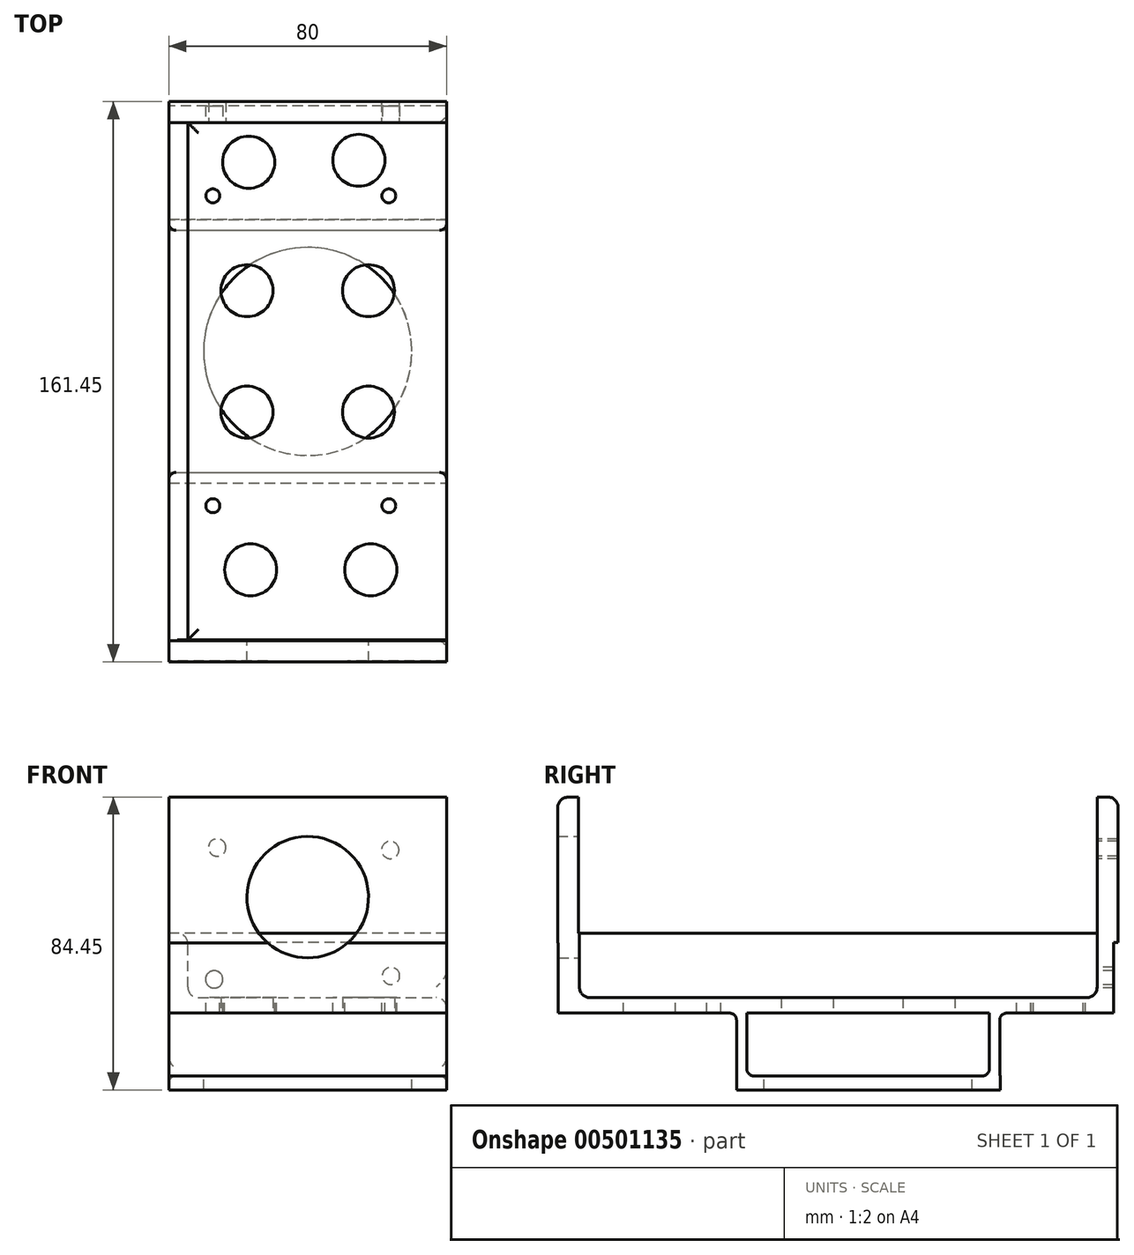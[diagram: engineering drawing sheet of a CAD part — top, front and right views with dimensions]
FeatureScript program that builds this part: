
annotation { "Feature Type Name" : "Feature", "Feature Type Description" : "" }
export const myFeature = defineFeature(function(context is Context, id is Id, definition is map)
    precondition{}
    {
        {
            var Q0;
            Q0=qCreatedBy(makeId("Right.planeOp"),FACE);
            cPlane(context, id + "F0", {"entities" : qUnion([Q0]), "cplaneType" : CPlaneType.OFFSET, "offset" : 40 * mm, "width" : 150 * mm, "height" : 150 * mm});
        }
        {
            var Q0;
            Q0=qCreatedBy(id+"F0.planeOp",FACE);
            var sketch = newSketch(context, id + "F1", { "sketchPlane" : qUnion([Q0])});
            skLineSegment(sketch, "E0.bottom", {"start": v(-37.9, -30.8) * mm, "end": v(38.1, -30.8) * mm});
            skLineSegment(sketch, "E0.top", {"start": v(-37.9, -34.8) * mm, "end": v(38.1, -34.8) * mm});
            skLineSegment(sketch, "E0.left", {"start": v(-37.9, -30.8) * mm, "end": v(-37.9, -34.8) * mm});
            skLineSegment(sketch, "E0.right", {"start": v(38.1, -30.8) * mm, "end": v(38.1, -34.8) * mm});
            skLineSegment(sketch, "E1.bottom", {"start": v(-37.92, -9.8) * mm, "end": v(-34.92, -9.8) * mm});
            skLineSegment(sketch, "E1.top", {"start": v(-37.92, -30.8) * mm, "end": v(-34.92, -30.8) * mm});
            skLineSegment(sketch, "E1.left", {"start": v(-37.92, -9.8) * mm, "end": v(-37.92, -30.8) * mm});
            skLineSegment(sketch, "E1.right", {"start": v(-34.92, -9.8) * mm, "end": v(-34.92, -30.8) * mm});
            skLineSegment(sketch, "E2.MirrorCS", {"start": v(34.92, -9.8) * mm, "end": v(34.92, -30.8) * mm});
            skLineSegment(sketch, "E3.MirrorCS", {"start": v(37.92, -9.8) * mm, "end": v(34.92, -9.8) * mm});
            skLineSegment(sketch, "E4.MirrorCS", {"start": v(37.92, -9.8) * mm, "end": v(37.92, -30.8) * mm});
            skLineSegment(sketch, "E5.MirrorCS", {"start": v(37.92, -30.8) * mm, "end": v(34.92, -30.8) * mm});
            skLineSegment(sketch, "E6.bottom", {"start": v(-89.28, 10.32) * mm, "end": v(70.72, 10.32) * mm});
            skLineSegment(sketch, "E6.top", {"start": v(-89.28, -12.68) * mm, "end": v(70.72, -12.68) * mm});
            skLineSegment(sketch, "E6.left", {"start": v(-89.28, 10.32) * mm, "end": v(-89.28, -12.68) * mm});
            skLineSegment(sketch, "E6.right", {"start": v(70.72, 10.32) * mm, "end": v(70.72, -12.68) * mm});
            skSolve(sketch);
        }
        {
            var Q0;
            Q0=qSketchRegion(id+"F1",true);
            var Q1;
            Q1=qConstructionFilter(qBodyType(qCreatedBy(id+"F1",EDGE),BodyType.WIRE),ConstructionObject.NO);
            extrude(context, id + "F2", {"entities" : qUnion([Q0]), "surfaceEntities" : qUnion([Q1]), "oppositeDirection" : true, "depth" : 80 * mm});
        }
        {
            var Q0;
            Q0=qCreatedBy(makeId("Top.planeOp"),FACE);
            cPlane(context, id + "F3", {"entities" : qUnion([Q0]), "cplaneType" : CPlaneType.OFFSET, "offset" : 44.8 * mm, "width" : 150 * mm, "height" : 150 * mm});
        }
        {
            var Q0;
            Q0=makeQuery(id+"F2.opExtrude","SWEPT_EDGE",EDGE,{"disambiguationData":[OSD([sQuery(id+"F1.wireOp",EDGE,"8911faaa-2e56-4fcc-9375-60c6f1163b9a0.MirrorCS"),sQuery(id+"F1.wireOp",EDGE,"a3ff945b-d483-49d8-b67e-3c9789cdbadf0.MirrorCS")])]});
            var Q1;
            Q1=makeQuery(id+"F2.opExtrude","SWEPT_EDGE",EDGE,{"disambiguationData":[OSD([sQuery(id+"F1.wireOp",EDGE,"KpOeElVU-bQIC-6Ijm-ua4u-k8ctu78gNPEQ.bottom"),sQuery(id+"F1.wireOp",EDGE,"KpOeElVU-bQIC-6Ijm-ua4u-k8ctu78gNPEQ.right")])]});
            var Q2;
            Q2=makeQuery(id+"F2.opExtrude","SWEPT_EDGE",EDGE,{"disambiguationData":[OSD([sQuery(id+"F1.wireOp",EDGE,"E0.bottom"),sQuery(id+"F1.wireOp",EDGE,"E5.MirrorCS"),sQuery(id+"F1.wireOp",EDGE,"E2.MirrorCS")])]});
            var Q3;
            Q3=makeQuery(id+"F2.opExtrude","SWEPT_EDGE",EDGE,{"disambiguationData":[OSD([sQuery(id+"F1.wireOp",EDGE,"E0.bottom"),sQuery(id+"F1.wireOp",EDGE,"E1.top"),sQuery(id+"F1.wireOp",EDGE,"E1.right")])]});
            var Q4;
            Q4=makeQuery(id+"F2.opExtrude","SWEPT_EDGE",EDGE,{"disambiguationData":[OSD([sQuery(id+"F1.wireOp",EDGE,"E1.left"),sQuery(id+"F1.wireOp",EDGE,"KpOeElVU-bQIC-6Ijm-ua4u-k8ctu78gNPEQ.top")])]});
            var Q5;
            Q5=makeQuery(id+"F2.opExtrude","SWEPT_EDGE",EDGE,{"disambiguationData":[OSD([sQuery(id+"F1.wireOp",EDGE,"E4.MirrorCS"),sQuery(id+"F1.wireOp",EDGE,"63763e1a-3015-4774-828e-56aecf1c89e60.MirrorCS")])]});
            var Q6;
            {var subQ0=sQuery(id+"F1.wireOp",EDGE,"E0.bottom");Q6=makeQuery(id+"F2.opExtrude","CAP_EDGE",EDGE,{"disambiguationData":[OSD([subQ0]),TDD([makeQuery(id+"F1.imprint","IMPRINT",EDGE,{"disambiguationData":[TD([[makeQuery(id+"F1.imprint","INTERSECT",VERTEX,{"derivedFrom":[subQ0,sQuery(id+"F1.wireOp",EDGE,"E1.top"),sQuery(id+"F1.wireOp",EDGE,"E1.right")]}),-1.0]])],"derivedFrom":subQ0})])],"isStart":false});}
            var Q7;
            {var subQ0=sQuery(id+"F1.wireOp",EDGE,"E0.bottom");Q7=makeQuery(id+"F2.opExtrude","CAP_EDGE",EDGE,{"disambiguationData":[OSD([subQ0]),TDD([makeQuery(id+"F1.imprint","IMPRINT",EDGE,{"disambiguationData":[TD([[makeQuery(id+"F1.imprint","INTERSECT",VERTEX,{"derivedFrom":[subQ0,sQuery(id+"F1.wireOp",EDGE,"E1.top"),sQuery(id+"F1.wireOp",EDGE,"E1.right")]}),-1.0]])],"derivedFrom":subQ0})])],"isStart":true});}
            fillet(context, id + "F4", {"entities" : qUnion([Q0, Q1, Q2, Q3, Q4, Q5, Q6, Q7]), "radius" : 2 * mm, "tangentPropagation" : true, "allowEdgeOverflow" : false});
        }
        {
            var Q0;
            Q0=qCreatedBy(makeId("Top.planeOp"),FACE);
            cPlane(context, id + "F5", {"entities" : qUnion([Q0]), "cplaneType" : CPlaneType.OFFSET, "offset" : 12.9 * mm, "width" : 150 * mm, "height" : 150 * mm});
        }
        {
            var Q0;
            Q0=qCreatedBy(id+"F5.planeOp",FACE);
            var sketch = newSketch(context, id + "F6", { "sketchPlane" : qUnion([Q0])});
            skPoint(sketch, "E7", {"position": v(-27.34, 44.84) * mm});
            skLineSegment(sketch, "E8", {"start": v(-2, 0.18) * mm, "end": v(-2, 48.05) * mm});
            skLineSegment(sketch, "E9", {"start": v(-2, 48.05) * mm, "end": v(-2, 0.18) * mm, "construction": true});
            skLineSegment(sketch, "E10", {"start": v(-2, 0.18) * mm, "end": v(-2, -49.46) * mm});
            skLineSegment(sketch, "E11", {"start": v(-2, 0.18) * mm, "end": v(39.06, 0.18) * mm});
            skLineSegment(sketch, "E12", {"start": v(39.06, 0.18) * mm, "end": v(-44.25, 0.18) * mm, "construction": true});
            skPoint(sketch, "E13.MirrorP", {"position": v(23.36, 44.84) * mm});
            skLineSegment(sketch, "E14.MirrorCS", {"start": v(-2, 0.18) * mm, "end": v(-2, -49.46) * mm, "construction": true});
            skPoint(sketch, "E15.MirrorP", {"position": v(-27.34, -44.5) * mm});
            skPoint(sketch, "E16.MirrorP", {"position": v(23.36, -44.5) * mm});
            skSolve(sketch);
        }
        {
            var Q0;
            Q0=sQuery(id+"F6.wireOp",VERTEX,"E16.MirrorP");
            var Q1;
            Q1=sQuery(id+"F6.wireOp",VERTEX,"E15.MirrorP");
            var Q2;
            Q2=sQuery(id+"F6.wireOp",VERTEX,"E7");
            var Q3;
            Q3=sQuery(id+"F6.wireOp",VERTEX,"E13.MirrorP");
            var Q4;
            Q4=makeQuery(id+"F2.opExtrude","SWEPT_BODY",BODY,{"disambiguationData":[OSD([sQuery(id+"F1.wireOp",EDGE,"E0.bottom"),sQuery(id+"F1.wireOp",EDGE,"E0.top"),sQuery(id+"F1.wireOp",EDGE,"E0.left"),sQuery(id+"F1.wireOp",EDGE,"E0.right"),sQuery(id+"F1.wireOp",EDGE,"E1.top"),sQuery(id+"F1.wireOp",EDGE,"E1.left"),sQuery(id+"F1.wireOp",EDGE,"E1.right"),sQuery(id+"F1.wireOp",EDGE,"E4.MirrorCS"),sQuery(id+"F1.wireOp",EDGE,"E2.MirrorCS"),sQuery(id+"F1.wireOp",EDGE,"E6.bottom"),sQuery(id+"F1.wireOp",EDGE,"E6.top"),sQuery(id+"F1.wireOp",EDGE,"E6.left"),sQuery(id+"F1.wireOp",EDGE,"E6.right")])]});
            hole(context, id + "F7", {"style" : HoleStyle.SIMPLE, "endStyle" : HoleEndStyle.BLIND, "holeDiameter" : 4 * mm, "holeDepth" : 25 * mm, "isTappedThrough" : true, "tappedDepth" : 12 * mm, "tapClearance" : 3, "locations" : qUnion([Q0, Q1, Q2, Q3]), "scope" : qUnion([Q4])});
        }
        {
            var Q0;
            Q0=qCreatedBy(makeId("Top.planeOp"),FACE);
            cPlane(context, id + "F8", {"entities" : qUnion([Q0]), "cplaneType" : CPlaneType.OFFSET, "offset" : 12.8 * mm, "width" : 150 * mm, "height" : 150 * mm});
        }
        {
            var Q0;
            Q0=qCreatedBy(id+"F8.planeOp",FACE);
            var sketch = newSketch(context, id + "F9", { "sketchPlane" : qUnion([Q0])});
            skLineSegment(sketch, "E17.bottom", {"start": v(-39.53, 72.98) * mm, "end": v(-34.53, 72.98) * mm, "construction": true});
            skLineSegment(sketch, "E17.top", {"start": v(-39.53, 65.98) * mm, "end": v(-34.53, 65.98) * mm, "construction": true});
            skLineSegment(sketch, "E17.left", {"start": v(-39.53, 72.98) * mm, "end": v(-39.53, 65.98) * mm, "construction": true});
            skLineSegment(sketch, "E17.right", {"start": v(-34.53, 72.98) * mm, "end": v(-34.53, 65.98) * mm, "construction": true});
            skLineSegment(sketch, "E18.bottom", {"start": v(-40.05, -95.1) * mm, "end": v(-35.05, -95.1) * mm, "construction": true});
            skLineSegment(sketch, "E18.top", {"start": v(-40.05, -102.1) * mm, "end": v(-35.05, -102.1) * mm, "construction": true});
            skLineSegment(sketch, "E18.left", {"start": v(-40.05, -95.1) * mm, "end": v(-40.05, -102.1) * mm, "construction": true});
            skLineSegment(sketch, "E18.right", {"start": v(-35.05, -95.1) * mm, "end": v(-35.05, -102.1) * mm, "construction": true});
            skLineSegment(sketch, "E19.bottom", {"start": v(40.15, 72.98) * mm, "end": v(47.15, 72.98) * mm, "construction": true});
            skLineSegment(sketch, "E19.top", {"start": v(40.15, 65.98) * mm, "end": v(47.15, 65.98) * mm, "construction": true});
            skLineSegment(sketch, "E19.left", {"start": v(40.15, 72.98) * mm, "end": v(40.15, 65.98) * mm, "construction": true});
            skLineSegment(sketch, "E19.right", {"start": v(47.15, 72.98) * mm, "end": v(47.15, 65.98) * mm, "construction": true});
            skLineSegment(sketch, "E20.bottom", {"start": v(-34.53, 65.98) * mm, "end": v(40.15, 65.98) * mm});
            skLineSegment(sketch, "E20.top", {"start": v(-34.53, -83.16) * mm, "end": v(40.15, -83.16) * mm});
            skLineSegment(sketch, "E20.left", {"start": v(-34.53, 65.98) * mm, "end": v(-34.53, -83.16) * mm});
            skLineSegment(sketch, "E20.right", {"start": v(40.15, 65.98) * mm, "end": v(40.15, -83.16) * mm});
            skSolve(sketch);
        }
        {
            var Q0;
            Q0 = qSketchRegion(id + "F9", true);
            extrude(context, id + "F10", {"entities" : qUnion([Q0]), "operationType" : NewBodyOperationType.REMOVE, "oppositeDirection" : true, "depth" : 21 * mm});
        }
        {
            var Q0;
            Q0=qCreatedBy(makeId("Right.planeOp"),FACE);
            var sketch = newSketch(context, id + "F11", { "sketchPlane" : qUnion([Q0])});
            skLineSegment(sketch, "E21.bottom", {"start": v(-89.45, 7.56) * mm, "end": v(-83.45, 7.56) * mm});
            skLineSegment(sketch, "E21.top", {"start": v(-89.45, 49.56) * mm, "end": v(-83.45, 49.56) * mm});
            skLineSegment(sketch, "E21.left", {"start": v(-89.45, 7.56) * mm, "end": v(-89.45, 49.56) * mm});
            skLineSegment(sketch, "E21.right", {"start": v(-83.45, 7.56) * mm, "end": v(-83.45, 49.56) * mm});
            skLineSegment(sketch, "E22.bottom", {"start": v(66, 7.64) * mm, "end": v(72, 7.64) * mm});
            skLineSegment(sketch, "E22.top", {"start": v(66, 49.64) * mm, "end": v(72, 49.64) * mm});
            skLineSegment(sketch, "E22.left", {"start": v(66, 7.64) * mm, "end": v(66, 49.64) * mm});
            skLineSegment(sketch, "E22.right", {"start": v(72, 7.64) * mm, "end": v(72, 49.64) * mm});
            skSolve(sketch);
        }
        {
            var Q0;
            Q0 = qSketchRegion(id + "F11", true);
            extrude(context, id + "F12", {"entities" : qUnion([Q0]), "operationType" : NewBodyOperationType.ADD, "endBound" : BoundingType.SYMMETRIC, "depth" : 80 * mm});
        }
        {
            var Q0;
            Q0=qCreatedBy(makeId("Front.planeOp"),FACE);
            var sketch = newSketch(context, id + "F13", { "sketchPlane" : qUnion([Q0])});
            skCircle(sketch, "E23", {"center": v(-26.09, 35.07) * mm, "radius": 2.5 * mm});
            skLineSegment(sketch, "E24", {"start": v(-26.09, 23.89) * mm, "end": v(-26.09, 0) * mm, "construction": true});
            skLineSegment(sketch, "E25", {"start": v(23.77, 22.73) * mm, "end": v(23.92, 0) * mm, "construction": true});
            skCircle(sketch, "E26", {"center": v(-26.95, -2.95) * mm, "radius": 2.5 * mm});
            skLineSegment(sketch, "E27", {"start": v(-26.95, 1.86) * mm, "end": v(-26.95, -22.03) * mm, "construction": true});
            skLineSegment(sketch, "E28", {"start": v(23.77, 12.22) * mm, "end": v(24, -22.03) * mm, "construction": true});
            skCircle(sketch, "E29", {"center": v(23.77, 34.34) * mm, "radius": 2.5 * mm});
            skLineSegment(sketch, "E30", {"start": v(23.77, 24.59) * mm, "end": v(23.77, 12.22) * mm, "construction": true});
            skLineSegment(sketch, "E31", {"start": v(74.64, 23.43) * mm, "end": v(74.78, 0.7) * mm, "construction": true});
            skCircle(sketch, "E32", {"center": v(23.98, -1.95) * mm, "radius": 2.5 * mm});
            skLineSegment(sketch, "E33", {"start": v(23.98, 2.86) * mm, "end": v(23.98, -21.03) * mm, "construction": true});
            skLineSegment(sketch, "E34", {"start": v(74.78, 1.7) * mm, "end": v(74.92, -21.03) * mm, "construction": true});
            skPoint(sketch, "E35", {"position": v(0, 20.75) * mm});
            skSolve(sketch);
        }
        {
            var Q0;
            Q0=makeQuery(id+"F12.opExtrude","SWEPT_EDGE",EDGE,{"disambiguationData":[OSD([sQuery(id+"F11.wireOp",EDGE,"E21.top"),sQuery(id+"F11.wireOp",EDGE,"E21.left")])]});
            var Q1;
            Q1=makeQuery(id+"F10.boolean.opBoolean","COPY",EDGE,{"derivedFrom":makeQuery(id+"F10.opExtrude","CAP_EDGE",EDGE,{"disambiguationData":[OSD([sQuery(id+"F9.wireOp",EDGE,"E20.top")])],"isStart":false})});
            var Q2;
            Q2=makeQuery(id+"F10.boolean.opBoolean","COPY",EDGE,{"derivedFrom":makeQuery(id+"F10.opExtrude","CAP_EDGE",EDGE,{"disambiguationData":[OSD([sQuery(id+"F9.wireOp",EDGE,"E20.left")])],"isStart":false})});
            var Q3;
            Q3=makeQuery(id+"F10.boolean.opBoolean","INTERSECT",EDGE,{"derivedFrom":[makeQuery(id+"F2.opExtrude","CAP_FACE",FACE,{"disambiguationData":[OSD([sQuery(id+"F1.wireOp",EDGE,"E0.bottom"),sQuery(id+"F1.wireOp",EDGE,"E0.top"),sQuery(id+"F1.wireOp",EDGE,"E0.left"),sQuery(id+"F1.wireOp",EDGE,"E0.right"),sQuery(id+"F1.wireOp",EDGE,"E1.top"),sQuery(id+"F1.wireOp",EDGE,"E1.left"),sQuery(id+"F1.wireOp",EDGE,"E1.right"),sQuery(id+"F1.wireOp",EDGE,"E4.MirrorCS"),sQuery(id+"F1.wireOp",EDGE,"E2.MirrorCS"),sQuery(id+"F1.wireOp",EDGE,"E6.bottom"),sQuery(id+"F1.wireOp",EDGE,"E6.top"),sQuery(id+"F1.wireOp",EDGE,"E6.left"),sQuery(id+"F1.wireOp",EDGE,"E6.right")])],"isStart":true}),makeQuery(id+"F10.opExtrude","CAP_FACE",FACE,{"disambiguationData":[OSD([sQuery(id+"F9.wireOp",EDGE,"E20.bottom"),sQuery(id+"F9.wireOp",EDGE,"E20.top"),sQuery(id+"F9.wireOp",EDGE,"E20.left"),sQuery(id+"F9.wireOp",EDGE,"E20.right")])],"isStart":false})]});
            var Q4;
            Q4=makeQuery(id+"F10.boolean.opBoolean","INTERSECT",EDGE,{"derivedFrom":[makeQuery(id+"F2.opExtrude","SWEPT_FACE",FACE,{"disambiguationData":[OSD([sQuery(id+"F1.wireOp",EDGE,"E6.bottom")])]}),makeQuery(id+"F10.opExtrude","SWEPT_FACE",FACE,{"disambiguationData":[OSD([sQuery(id+"F9.wireOp",EDGE,"E20.left")])]})]});
            var Q5;
            Q5=makeQuery(id+"F12.opExtrude","SWEPT_EDGE",EDGE,{"disambiguationData":[OSD([sQuery(id+"F11.wireOp",EDGE,"E22.top"),sQuery(id+"F11.wireOp",EDGE,"E22.right")])]});
            var Q6;
            Q6=makeQuery(id+"F10.boolean.opBoolean","COPY",EDGE,{"derivedFrom":makeQuery(id+"F10.opExtrude","CAP_EDGE",EDGE,{"disambiguationData":[OSD([sQuery(id+"F9.wireOp",EDGE,"E20.bottom")])],"isStart":false})});
            fillet(context, id + "F14", {"entities" : qUnion([Q0, Q1, Q2, Q3, Q4, Q5, Q6]), "radius" : 3 * mm, "tangentPropagation" : true, "allowEdgeOverflow" : false});
        }
        {
            var Q0;
            Q0=sQuery(id+"F13.wireOp",VERTEX,"E29.center");
            var Q1;
            Q1=sQuery(id+"F13.wireOp",VERTEX,"E32.center");
            var Q2;
            Q2=sQuery(id+"F13.wireOp",VERTEX,"E26.center");
            var Q3;
            Q3=sQuery(id+"F13.wireOp",VERTEX,"E23.center");
            var Q4;
            Q4=makeQuery(id+"F2.opExtrude","SWEPT_BODY",BODY,{"disambiguationData":[OSD([sQuery(id+"F1.wireOp",EDGE,"E0.bottom"),sQuery(id+"F1.wireOp",EDGE,"E0.top"),sQuery(id+"F1.wireOp",EDGE,"E0.left"),sQuery(id+"F1.wireOp",EDGE,"E0.right"),sQuery(id+"F1.wireOp",EDGE,"E1.top"),sQuery(id+"F1.wireOp",EDGE,"E1.left"),sQuery(id+"F1.wireOp",EDGE,"E1.right"),sQuery(id+"F1.wireOp",EDGE,"E4.MirrorCS"),sQuery(id+"F1.wireOp",EDGE,"E2.MirrorCS"),sQuery(id+"F1.wireOp",EDGE,"E6.bottom"),sQuery(id+"F1.wireOp",EDGE,"E6.top"),sQuery(id+"F1.wireOp",EDGE,"E6.left"),sQuery(id+"F1.wireOp",EDGE,"E6.right")])]});
            hole(context, id + "F15", {"style" : HoleStyle.SIMPLE, "endStyle" : HoleEndStyle.THROUGH, "holeDiameter" : 5 * mm, "isTappedThrough" : true, "tappedDepth" : 12 * mm, "tapClearance" : 3, "locations" : qUnion([Q0, Q1, Q2, Q3]), "scope" : qUnion([Q4])});
        }
        {
            var Q0;
            Q0=sQuery(id+"F13.wireOp",VERTEX,"E35");
            var Q1;
            Q1=makeQuery(id+"F2.opExtrude","SWEPT_BODY",BODY,{"disambiguationData":[OSD([sQuery(id+"F1.wireOp",EDGE,"E0.bottom"),sQuery(id+"F1.wireOp",EDGE,"E0.top"),sQuery(id+"F1.wireOp",EDGE,"E0.left"),sQuery(id+"F1.wireOp",EDGE,"E0.right"),sQuery(id+"F1.wireOp",EDGE,"E1.top"),sQuery(id+"F1.wireOp",EDGE,"E1.left"),sQuery(id+"F1.wireOp",EDGE,"E1.right"),sQuery(id+"F1.wireOp",EDGE,"E4.MirrorCS"),sQuery(id+"F1.wireOp",EDGE,"E2.MirrorCS"),sQuery(id+"F1.wireOp",EDGE,"E6.bottom"),sQuery(id+"F1.wireOp",EDGE,"E6.top"),sQuery(id+"F1.wireOp",EDGE,"E6.left"),sQuery(id+"F1.wireOp",EDGE,"E6.right")])]});
            hole(context, id + "F16", {"style" : HoleStyle.SIMPLE, "endStyle" : HoleEndStyle.THROUGH, "oppositeDirection" : true, "holeDiameter" : 35 * mm, "isTappedThrough" : true, "tappedDepth" : 12 * mm, "tapClearance" : 3, "locations" : qUnion([Q0]), "scope" : qUnion([Q1])});
        }
        {
            var Q0;
            Q0=qCreatedBy(makeId("Top.planeOp"),FACE);
            cPlane(context, id + "F17", {"entities" : qUnion([Q0]), "cplaneType" : CPlaneType.OFFSET, "offset" : 30.3 * mm, "oppositeDirection" : true, "width" : 150 * mm, "height" : 150 * mm});
        }
        {
            var Q0;
            Q0=qCreatedBy(id+"F17.planeOp",FACE);
            var sketch = newSketch(context, id + "F18", { "sketchPlane" : qUnion([Q0])});
            skPoint(sketch, "E36", {"position": v(0, 0) * mm});
            skLineSegment(sketch, "E37.bottom", {"start": v(17.5, 17.5) * mm, "end": v(-17.5, 17.5) * mm, "construction": true});
            skLineSegment(sketch, "E37.top", {"start": v(17.5, -17.5) * mm, "end": v(-17.5, -17.5) * mm, "construction": true});
            skLineSegment(sketch, "E37.left", {"start": v(17.5, 17.5) * mm, "end": v(17.5, -17.5) * mm, "construction": true});
            skLineSegment(sketch, "E37.right", {"start": v(-17.5, 17.5) * mm, "end": v(-17.5, -17.5) * mm, "construction": true});
            skSolve(sketch);
        }
        {
            var Q0;
            Q0=sQuery(id+"F18.wireOp",VERTEX,"E36");
            var Q1;
            Q1=makeQuery(id+"F2.opExtrude","SWEPT_BODY",BODY,{"disambiguationData":[OSD([sQuery(id+"F1.wireOp",EDGE,"E0.bottom"),sQuery(id+"F1.wireOp",EDGE,"E0.top"),sQuery(id+"F1.wireOp",EDGE,"E0.left"),sQuery(id+"F1.wireOp",EDGE,"E0.right"),sQuery(id+"F1.wireOp",EDGE,"E1.top"),sQuery(id+"F1.wireOp",EDGE,"E1.left"),sQuery(id+"F1.wireOp",EDGE,"E1.right"),sQuery(id+"F1.wireOp",EDGE,"E4.MirrorCS"),sQuery(id+"F1.wireOp",EDGE,"E2.MirrorCS"),sQuery(id+"F1.wireOp",EDGE,"E6.bottom"),sQuery(id+"F1.wireOp",EDGE,"E6.top"),sQuery(id+"F1.wireOp",EDGE,"E6.left"),sQuery(id+"F1.wireOp",EDGE,"E6.right")])]});
            hole(context, id + "F19", {"style" : HoleStyle.SIMPLE, "endStyle" : HoleEndStyle.THROUGH, "holeDiameter" : 60 * mm, "isTappedThrough" : true, "tappedDepth" : 12 * mm, "tapClearance" : 3, "locations" : qUnion([Q0]), "scope" : qUnion([Q1])});
        }
        {
            var Q0;
            Q0=sQuery(id+"F18.wireOp",VERTEX,"E37.right.end");
            var Q1;
            Q1=sQuery(id+"F18.wireOp",VERTEX,"E37.left.end");
            var Q2;
            Q2=sQuery(id+"F18.wireOp",VERTEX,"E37.left.start");
            var Q3;
            Q3=sQuery(id+"F18.wireOp",VERTEX,"E37.right.start");
            var Q4;
            Q4=makeQuery(id+"F2.opExtrude","SWEPT_BODY",BODY,{"disambiguationData":[OSD([sQuery(id+"F1.wireOp",EDGE,"E0.bottom"),sQuery(id+"F1.wireOp",EDGE,"E0.top"),sQuery(id+"F1.wireOp",EDGE,"E0.left"),sQuery(id+"F1.wireOp",EDGE,"E0.right"),sQuery(id+"F1.wireOp",EDGE,"E1.top"),sQuery(id+"F1.wireOp",EDGE,"E1.left"),sQuery(id+"F1.wireOp",EDGE,"E1.right"),sQuery(id+"F1.wireOp",EDGE,"E4.MirrorCS"),sQuery(id+"F1.wireOp",EDGE,"E2.MirrorCS"),sQuery(id+"F1.wireOp",EDGE,"E6.bottom"),sQuery(id+"F1.wireOp",EDGE,"E6.top"),sQuery(id+"F1.wireOp",EDGE,"E6.left"),sQuery(id+"F1.wireOp",EDGE,"E6.right")])]});
            hole(context, id + "F20", {"style" : HoleStyle.SIMPLE, "endStyle" : HoleEndStyle.THROUGH, "oppositeDirection" : true, "holeDiameter" : 15 * mm, "isTappedThrough" : true, "tappedDepth" : 12 * mm, "tapClearance" : 3, "locations" : qUnion([Q0, Q1, Q2, Q3]), "scope" : qUnion([Q4])});
        }
        {
            var Q0;
            Q0=qCreatedBy(makeId("Top.planeOp"),FACE);
            var sketch = newSketch(context, id + "F21", { "sketchPlane" : qUnion([Q0])});
            skCircle(sketch, "E38", {"center": v(-16.44, -62.97) * mm, "radius": 7.5 * mm, "construction": true});
            skCircle(sketch, "E39", {"center": v(18.15, -62.97) * mm, "radius": 7.5 * mm, "construction": true});
            skCircle(sketch, "E40", {"center": v(-17, 54.52) * mm, "radius": 7.5 * mm, "construction": true});
            skCircle(sketch, "E41", {"center": v(14.72, 55.1) * mm, "radius": 7.5 * mm, "construction": true});
            skSolve(sketch);
        }
        {
            var Q0;
            Q0=sQuery(id+"F21.wireOp",VERTEX,"E39.center");
            var Q1;
            Q1=sQuery(id+"F21.wireOp",VERTEX,"E38.center");
            var Q2;
            Q2=sQuery(id+"F21.wireOp",VERTEX,"E40.center");
            var Q3;
            Q3=sQuery(id+"F21.wireOp",VERTEX,"E41.center");
            var Q4;
            Q4=makeQuery(id+"F2.opExtrude","SWEPT_BODY",BODY,{"disambiguationData":[OSD([sQuery(id+"F1.wireOp",EDGE,"E0.bottom"),sQuery(id+"F1.wireOp",EDGE,"E0.top"),sQuery(id+"F1.wireOp",EDGE,"E0.left"),sQuery(id+"F1.wireOp",EDGE,"E0.right"),sQuery(id+"F1.wireOp",EDGE,"E1.top"),sQuery(id+"F1.wireOp",EDGE,"E1.left"),sQuery(id+"F1.wireOp",EDGE,"E1.right"),sQuery(id+"F1.wireOp",EDGE,"E4.MirrorCS"),sQuery(id+"F1.wireOp",EDGE,"E2.MirrorCS"),sQuery(id+"F1.wireOp",EDGE,"E6.bottom"),sQuery(id+"F1.wireOp",EDGE,"E6.top"),sQuery(id+"F1.wireOp",EDGE,"E6.left"),sQuery(id+"F1.wireOp",EDGE,"E6.right")])]});
            hole(context, id + "F22", {"style" : HoleStyle.SIMPLE, "endStyle" : HoleEndStyle.THROUGH, "holeDiameter" : 15 * mm, "isTappedThrough" : true, "tappedDepth" : 12 * mm, "tapClearance" : 3, "locations" : qUnion([Q0, Q1, Q2, Q3]), "scope" : qUnion([Q4])});
        }
    });
